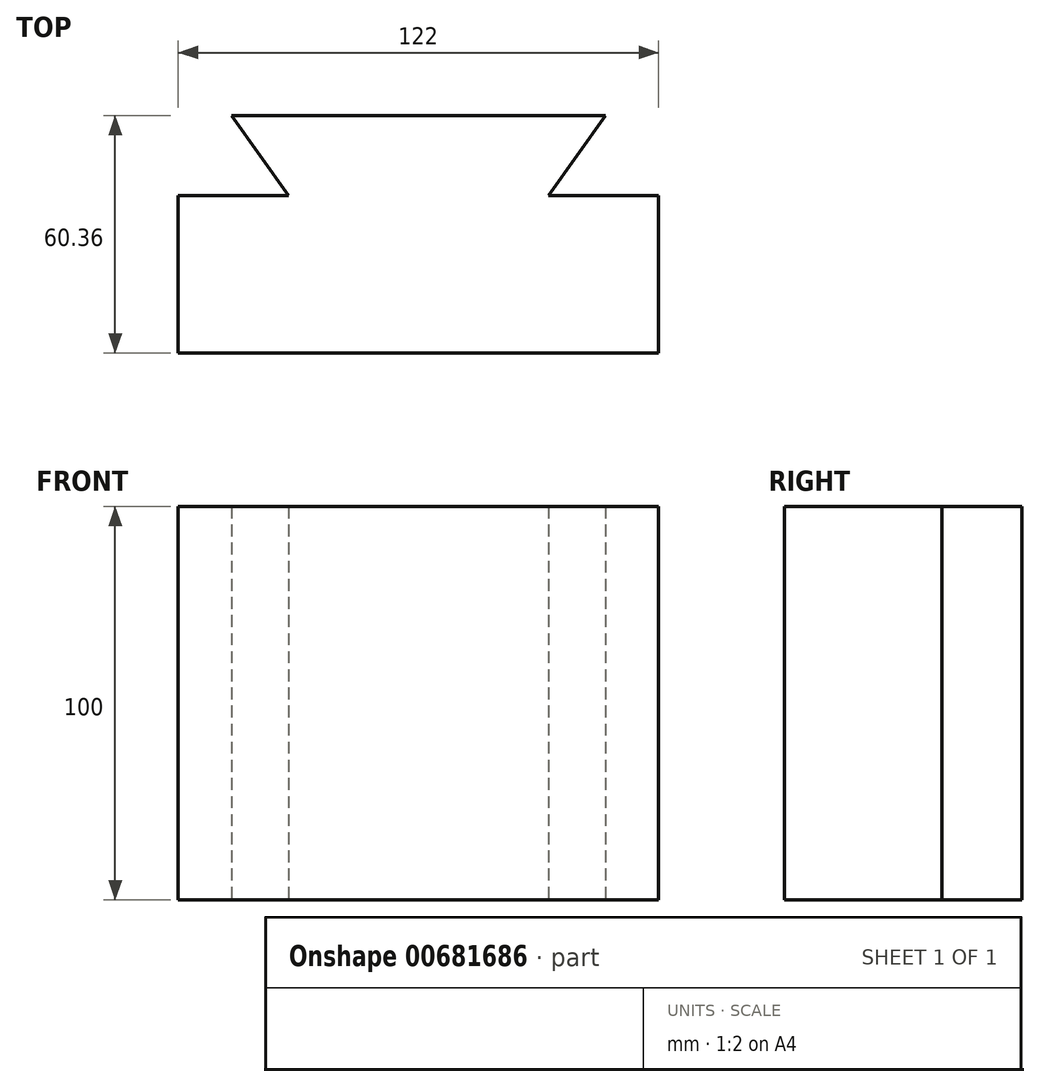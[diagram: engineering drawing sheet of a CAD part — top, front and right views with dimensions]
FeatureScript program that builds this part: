
annotation { "Feature Type Name" : "Feature", "Feature Type Description" : "" }
export const myFeature = defineFeature(function(context is Context, id is Id, definition is map)
    precondition{}
    {
        {
            var Q0;
            Q0=qCreatedBy(makeId("Top.planeOp"),FACE);
            var sketch = newSketch(context, id + "F0", { "sketchPlane" : qUnion([Q0])});
            skLineSegment(sketch, "E0", {"start": v(-54.9, 40.17) * mm, "end": v(40.1, 40.17) * mm});
            skLineSegment(sketch, "E1", {"start": v(40.1, 40.17) * mm, "end": v(25.6, 19.8) * mm});
            skLineSegment(sketch, "E2", {"start": v(25.6, 19.8) * mm, "end": v(53.6, 19.8) * mm});
            skLineSegment(sketch, "E3", {"start": v(53.6, 19.8) * mm, "end": v(53.6, -20.2) * mm});
            skLineSegment(sketch, "E4", {"start": v(-54.9, 40.17) * mm, "end": v(-40.4, 19.8) * mm});
            skLineSegment(sketch, "E5", {"start": v(-40.4, 19.8) * mm, "end": v(-68.4, 19.8) * mm});
            skLineSegment(sketch, "E6", {"start": v(-68.4, 19.8) * mm, "end": v(-68.4, -20.2) * mm});
            skLineSegment(sketch, "E7", {"start": v(-68.4, -20.2) * mm, "end": v(53.6, -20.2) * mm});
            skSolve(sketch);
        }
        {
            var Q0;
            Q0 = qSketchRegion(id + "F0", true);
            extrude(context, id + "F1", {"entities" : qUnion([Q0]), "depth" : 100 * mm, "offsetDistance" : 25 * mm});
        }
    });
